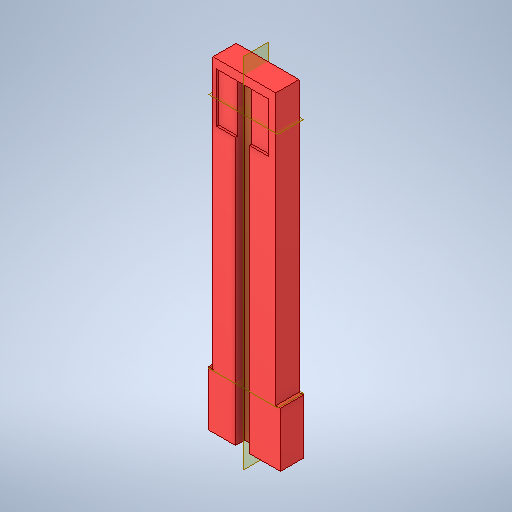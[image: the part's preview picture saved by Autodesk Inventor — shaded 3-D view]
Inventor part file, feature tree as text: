
AUTODESK INVENTOR PART (.ipt)
format: ipt  version: 2025 (Build 290162000, 162)  size: 310,784 bytes
history: native  units: mm
features: extrude x4, other x3, sketch x2, mirror x1, plane x1
ambient origin geometry x8: Origin, YZ Plane, XZ Plane, XY Plane, X Axis, Y Axis, Z Axis, Center Point
bodies: Body1 (feature_tree)
feature tree (11):
  extrude  "Extrusion3"  Depth=70.0mm TaperAngle=0.0deg
  extrude  "Extrusion5"  Depth=10.7mm
  extrude  "Extrusion6"  Depth=11.2mm
  other  "hor_Strahlebene"
  other  "Ebene_Anschlag2"
  extrude  "Extrusion8"  Depth=0.5mm TaperAngle=0.0deg
  other  "Mittelebene_Halter"
  mirror  "Spiegeln1"
  sketch  "Skizze4"  dims[d12=0.0mm d16=70.0mm d17=0.0mm]
  sketch  "Skizze10"  dims[d20=1.9mm d21=10.7mm d22=11.2mm d24=0.5mm d25=0.0mm d26=3.0mm d28=2.0mm d29=0.0mm d31=5.2mm d32=4.1mm d33=-51.0mm d36=1.0mm d37=10.0mm d38=0.0mm]
  plane  "Arbeitsebene4"
